# Revit family: WS_BARCELONA
name_source: partatom
category: Furniture
units: mm (PartAtom-declared; Revit-internal decimal feet)

## family parameters
Always vertical = Yes
Cut with Voids When Loaded = No
OmniClass Number = 23.40.20.00
OmniClass Title = General Furniture and Specialties
Room Calculation Point = No
Shared = No
Work Plane-Based = No

## types (18) — shared parameters
BS = No
BS-15 = No
BS-9 = No
BSP-15 = No
BSP-9 = No
BS_PASSTHROUGH = No
CER = No
CUTOUT_CENTER = No
CUTOUT_CENTER_CHECK = No
CUTOUT_SIDES = No
CUTOUT_SIDES_CHECK = No
FIXED = Yes
FX_MARINE_EDGE = No
HA = No
HA_MARINE_EDGE = No
MARINE_EDGE = No
Manufacturer = IBR Innovasystem
URL = https://ibr-innovasystem.com
WT_MATERIAL = Plástico, blanco opaco
WT_THICK = 16 mm  [stored 0.0524934 ft]
zero-valued in all types: Cost, Default Elevation

## per-type parameters (varying)
| type | COLUMN_H | Depth | Description | LOW_TAG | Length | WTheight_nominal | WTheight_real |
| WSBAR-1575918 | 1800 mm  [stored 5.90551 ft] | 750 mm  [stored 2.46063 ft] | WS Barcelona 1500x750x900/1800, 8xElectrical Outlets (Type TBD per project) | No | 1500 mm  [stored 4.92126 ft] | 900 mm  [stored 2.95276 ft] | 884 mm  [stored 2.90026 ft] |
| WSBAR-1575916 | 1570 mm | 750 mm  [stored 2.46063 ft] | WS Barcelona 1500x750x900/1570, 8xElectrical Outlets (Type TBD per project) | No | 1500 mm  [stored 4.92126 ft] | 900 mm  [stored 2.95276 ft] | 884 mm  [stored 2.90026 ft] |
| WSBAR-1275918 | 1800 mm  [stored 5.90551 ft] | 750 mm  [stored 2.46063 ft] | WS Barcelona 1200x750x900/1800, 8xElectrical Outlets (Type TBD per project) | No | 1200 mm  [stored 3.93701 ft] | 900 mm  [stored 2.95276 ft] | 884 mm  [stored 2.90026 ft] |
| WSBAR-1275916 | 1570 mm | 750 mm  [stored 2.46063 ft] | WS Barcelona 1200x750x900/1570, 8xElectrical Outlets (Type TBD per project) | No | 1200 mm  [stored 3.93701 ft] | 900 mm  [stored 2.95276 ft] | 884 mm  [stored 2.90026 ft] |
| WSBAR-0975916 | 1570 mm | 750 mm  [stored 2.46063 ft] | WS Barcelona 900x750x900/1570, 8xElectrical Outlets (Type TBD per project) | No | 900 mm  [stored 2.95276 ft] | 900 mm  [stored 2.95276 ft] | 884 mm  [stored 2.90026 ft] |
| WSBAR-0975918 | 1800 mm  [stored 5.90551 ft] | 750 mm  [stored 2.46063 ft] | WS Barcelona 900x750x900/1800, 8xElectrical Outlets (Type TBD per project) | No | 900 mm  [stored 2.95276 ft] | 900 mm  [stored 2.95276 ft] | 884 mm  [stored 2.90026 ft] |
| WSBAR-1590918 | 1800 mm  [stored 5.90551 ft] | 900 mm  [stored 2.95276 ft] | WS Barcelona 1500x900x900/1800, 8xElectrical Outlets (Type TBD per project) | No | 1500 mm  [stored 4.92126 ft] | 900 mm  [stored 2.95276 ft] | 884 mm  [stored 2.90026 ft] |
| WSBAR-1590916 | 1570 mm | 900 mm  [stored 2.95276 ft] | WS Barcelona 1500x900x900/1570, 8xElectrical Outlets (Type TBD per project) | No | 1500 mm  [stored 4.92126 ft] | 900 mm  [stored 2.95276 ft] | 884 mm  [stored 2.90026 ft] |
| WSBAR-1290918 | 1800 mm  [stored 5.90551 ft] | 900 mm  [stored 2.95276 ft] | WS Barcelona 1200x900x900/1800, 8xElectrical Outlets (Type TBD per project) | No | 1200 mm  [stored 3.93701 ft] | 900 mm  [stored 2.95276 ft] | 884 mm  [stored 2.90026 ft] |
| WSBAR-1290916 | 1570 mm | 900 mm  [stored 2.95276 ft] | WS Barcelona 1200x900x900/1570, 8xElectrical Outlets (Type TBD per project) | No | 1200 mm  [stored 3.93701 ft] | 900 mm  [stored 2.95276 ft] | 884 mm  [stored 2.90026 ft] |
| WSBAR-0990916 | 1570 mm | 900 mm  [stored 2.95276 ft] | WS Barcelona 900x900x900/1570, 8xElectrical Outlets (Type TBD per project) | No | 900 mm  [stored 2.95276 ft] | 900 mm  [stored 2.95276 ft] | 884 mm  [stored 2.90026 ft] |
| WSBAR-0990918 | 1800 mm  [stored 5.90551 ft] | 900 mm  [stored 2.95276 ft] | WS Barcelona 900x900x900/1800, 8xElectrical Outlets (Type TBD per project) | No | 900 mm  [stored 2.95276 ft] | 900 mm  [stored 2.95276 ft] | 884 mm  [stored 2.90026 ft] |
| WSBAR-1575716 | 1570 mm | 750 mm  [stored 2.46063 ft] | WS Barcelona 1500x750x750/1570, 8xElectrical Outlets (Type TBD per project) | Yes | 1500 mm  [stored 4.92126 ft] | 750 mm  [stored 2.46063 ft] | 734 mm  [stored 2.40814 ft] |
| WSBAR-1575718 | 1800 mm  [stored 5.90551 ft] | 750 mm  [stored 2.46063 ft] | WS Barcelona 1500x750x750/1800, 8xElectrical Outlets (Type TBD per project) | Yes | 1500 mm  [stored 4.92126 ft] | 750 mm  [stored 2.46063 ft] | 734 mm  [stored 2.40814 ft] |
| WSBAR-1275718 | 1800 mm  [stored 5.90551 ft] | 750 mm  [stored 2.46063 ft] | WS Barcelona 1200x750x750/1800, 8xElectrical Outlets (Type TBD per project) | Yes | 1200 mm  [stored 3.93701 ft] | 750 mm  [stored 2.46063 ft] | 734 mm  [stored 2.40814 ft] |
| WSBAR-1275716 | 1570 mm | 750 mm  [stored 2.46063 ft] | WS Barcelona 1200x750x750/1570, 8xElectrical Outlets (Type TBD per project) | Yes | 1200 mm  [stored 3.93701 ft] | 750 mm  [stored 2.46063 ft] | 734 mm  [stored 2.40814 ft] |
| WSBAR-0975716 | 1570 mm | 750 mm  [stored 2.46063 ft] | WS Barcelona 900x750x750/1570, 8xElectrical Outlets (Type TBD per project) | Yes | 900 mm  [stored 2.95276 ft] | 750 mm  [stored 2.46063 ft] | 734 mm  [stored 2.40814 ft] |
| WSBAR-0975718 | 1800 mm  [stored 5.90551 ft] | 750 mm  [stored 2.46063 ft] | WS Barcelona 900x750x750/1800, 8xElectrical Outlets (Type TBD per project) | Yes | 900 mm  [stored 2.95276 ft] | 750 mm  [stored 2.46063 ft] | 734 mm  [stored 2.40814 ft] |

note: [stored X ft] marks values corroborated as IEEE doubles in the binary element streams (Revit-internal decimal feet)

## geometry (parser evidence)
native form markers: Sweep x37
no freeform markers — native parametric forms only
